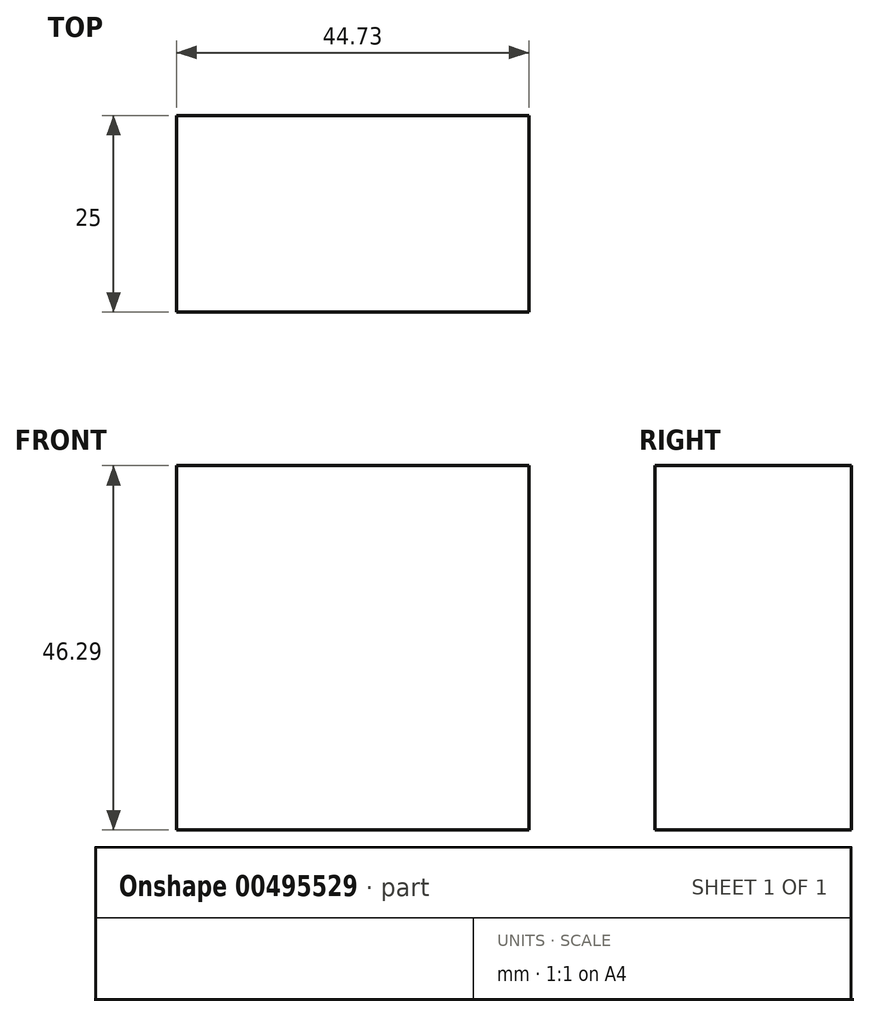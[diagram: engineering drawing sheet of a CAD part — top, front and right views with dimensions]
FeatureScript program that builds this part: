
annotation { "Feature Type Name" : "Feature", "Feature Type Description" : "" }
export const myFeature = defineFeature(function(context is Context, id is Id, definition is map)
    precondition{}
    {
        {
            var Q0;
            Q0=qCreatedBy(makeId("Front.planeOp"),FACE);
            var sketch = newSketch(context, id + "F0", { "sketchPlane" : qUnion([Q0])});
            skLineSegment(sketch, "E0.bottom", {"start": v(-90.8, 11.5) * mm, "end": v(-46.06, 11.5) * mm});
            skLineSegment(sketch, "E0.top", {"start": v(-90.8, 57.8) * mm, "end": v(-46.06, 57.8) * mm});
            skLineSegment(sketch, "E0.left", {"start": v(-90.8, 11.5) * mm, "end": v(-90.8, 57.8) * mm});
            skLineSegment(sketch, "E0.right", {"start": v(-46.06, 11.5) * mm, "end": v(-46.06, 57.8) * mm});
            skPoint(sketch, "E0.middle", {"position": v(-68.43, 34.65) * mm});
            skSolve(sketch);
        }
        {
            var Q0;
            Q0=makeQuery(id+"F0.imprint","IMPRINT",FACE,{"disambiguationData":[TD([[makeQuery(id+"F0.imprint","IMPRINT",EDGE,{"derivedFrom":sQuery(id+"F0.wireOp",EDGE,"E0.bottom")}),1.0]])]});
            extrude(context, id + "F1", {"entities" : qUnion([Q0]), "depth" : 25 * mm});
        }
    });
